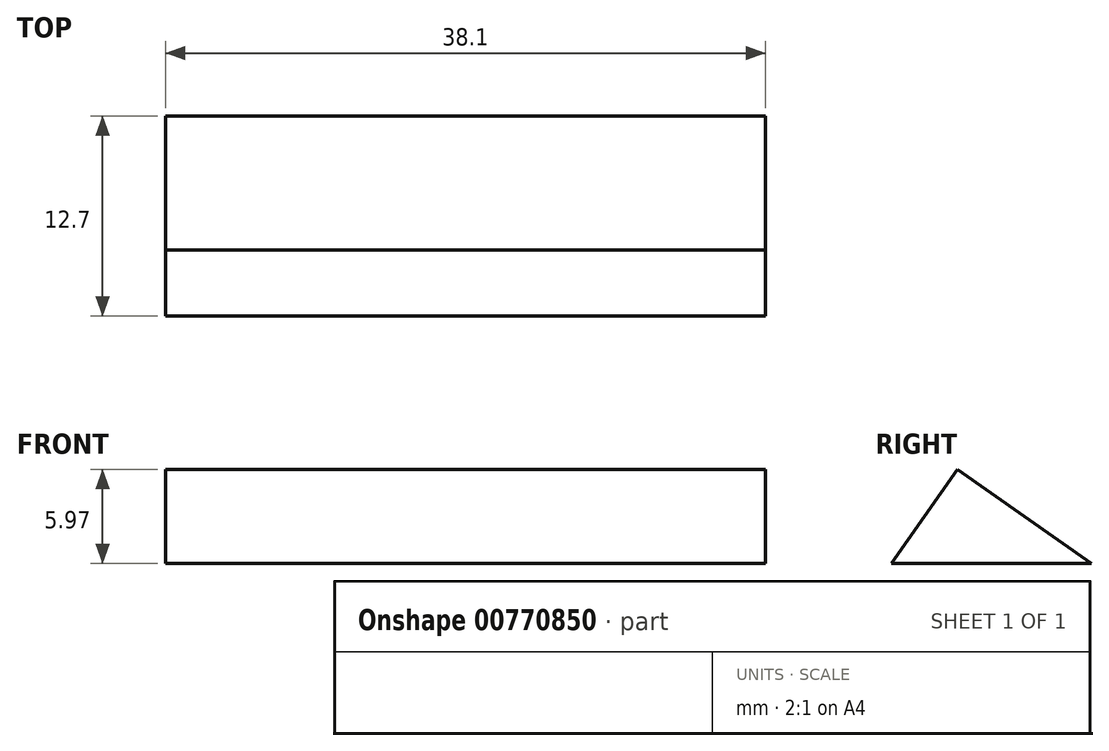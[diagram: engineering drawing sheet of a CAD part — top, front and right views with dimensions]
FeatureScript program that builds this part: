
annotation { "Feature Type Name" : "Feature", "Feature Type Description" : "" }
export const myFeature = defineFeature(function(context is Context, id is Id, definition is map)
    precondition{}
    {
        {
            var Q0;
            Q0=qCreatedBy(makeId("Right.planeOp"),FACE);
            var sketch = newSketch(context, id + "F0", { "sketchPlane" : qUnion([Q0])});
            skLineSegment(sketch, "E0", {"start": v(0, 0) * mm, "end": v(12.7, 0) * mm});
            skLineSegment(sketch, "E1", {"start": v(12.7, 0) * mm, "end": v(4.18, 5.97) * mm});
            skLineSegment(sketch, "E2", {"start": v(0, 0) * mm, "end": v(4.18, 5.97) * mm});
            skSolve(sketch);
        }
        {
            var Q0;
            Q0=makeQuery(id+"F0.imprint","IMPRINT",FACE,{"disambiguationData":[TD([[makeQuery(id+"F0.imprint","IMPRINT",EDGE,{"derivedFrom":sQuery(id+"F0.wireOp",EDGE,"E0")}),1.0]])]});
            extrude(context, id + "F1", {"entities" : qUnion([Q0]), "depth" : 38.1 * mm, "offsetDistance" : 25.4 * mm});
        }
    });
